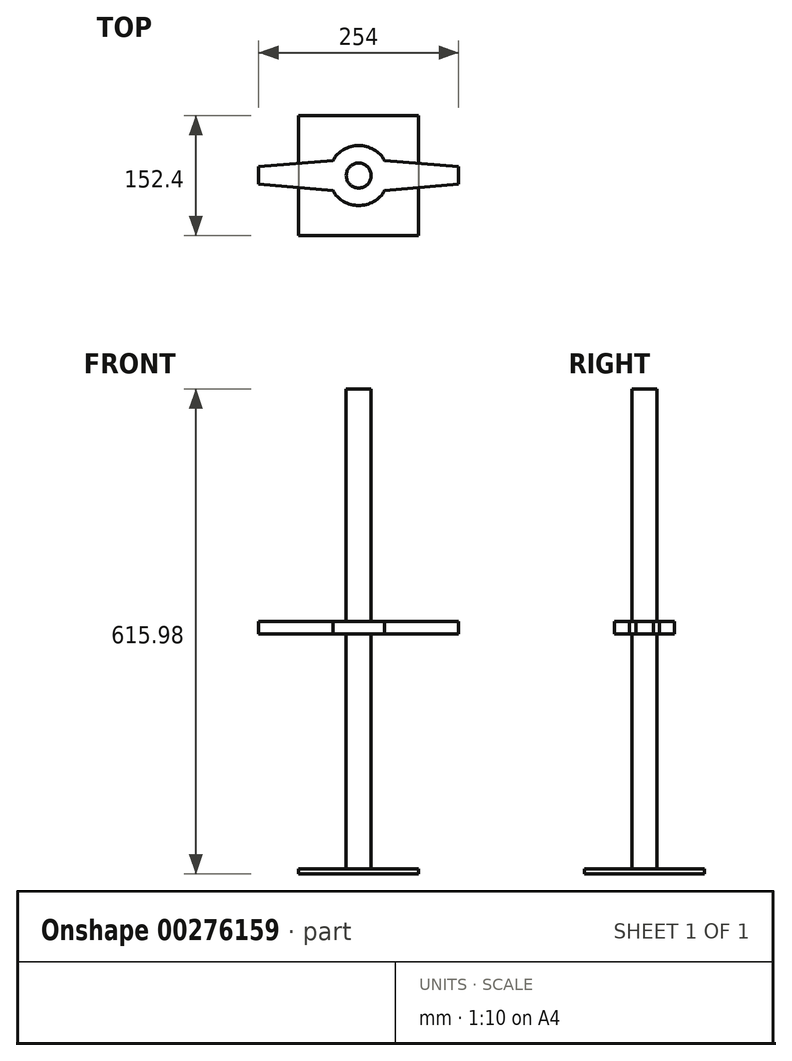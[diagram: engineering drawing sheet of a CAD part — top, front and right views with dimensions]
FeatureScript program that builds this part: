
annotation { "Feature Type Name" : "Feature", "Feature Type Description" : "" }
export const myFeature = defineFeature(function(context is Context, id is Id, definition is map)
    precondition{}
    {
        {
            var Q0;
            Q0=qCreatedBy(makeId("Top.planeOp"),FACE);
            var sketch = newSketch(context, id + "F0", { "sketchPlane" : qUnion([Q0])});
            skLineSegment(sketch, "E0.bottom", {"start": v(76.2, 76.2) * mm, "end": v(-76.2, 76.2) * mm});
            skLineSegment(sketch, "E0.top", {"start": v(76.2, -76.2) * mm, "end": v(-76.2, -76.2) * mm});
            skLineSegment(sketch, "E0.left", {"start": v(76.2, 76.2) * mm, "end": v(76.2, -76.2) * mm});
            skLineSegment(sketch, "E0.right", {"start": v(-76.2, 76.2) * mm, "end": v(-76.2, -76.2) * mm});
            skPoint(sketch, "E0.middle", {"position": v(0, 0) * mm});
            skSolve(sketch);
        }
        {
            var Q0;
            Q0 = qSketchRegion(id + "F0", true);
            extrude(context, id + "F1", {"entities" : qUnion([Q0]), "depth" : 6.38 * mm});
        }
        {
            var Q0;
            Q0=makeQuery(id+"F1.opExtrude","CAP_FACE",FACE,{"disambiguationData":[OSD([sQuery(id+"F0.wireOp",EDGE,"E0.bottom"),sQuery(id+"F0.wireOp",EDGE,"E0.top"),sQuery(id+"F0.wireOp",EDGE,"E0.left"),sQuery(id+"F0.wireOp",EDGE,"E0.right")])],"isStart":false});
            var sketch = newSketch(context, id + "F2", { "sketchPlane" : qUnion([Q0])});
            skCircle(sketch, "E1", {"center": v(0, 0) * mm, "radius": 15.88 * mm});
            skSolve(sketch);
        }
        {
            var Q0;
            Q0 = qSketchRegion(id + "F2", true);
            extrude(context, id + "F3", {"entities" : qUnion([Q0]), "operationType" : NewBodyOperationType.ADD, "depth" : 609.6 * mm});
        }
        {
            var Q0;
            Q0=qCreatedBy(makeId("Top.planeOp"),FACE);
            cPlane(context, id + "F4", {"entities" : qUnion([Q0]), "cplaneType" : CPlaneType.OFFSET, "offset" : 304.8 * mm, "width" : 152.4 * mm, "height" : 152.4 * mm});
        }
        {
            var Q0;
            Q0=qCreatedBy(id+"F4.planeOp",FACE);
            var sketch = newSketch(context, id + "F5", { "sketchPlane" : qUnion([Q0])});
            skArc(sketch, "E2", {"start": v(33, 19.05) * mm, "mid": v(0, 38.1) * mm, "end": v(-33, 19.05) * mm});
            skLineSegment(sketch, "E3", {"start": v(33, -19.05) * mm, "end": v(127, -11.11) * mm});
            skLineSegment(sketch, "E4", {"start": v(127, -11.11) * mm, "end": v(127, 11.11) * mm});
            skLineSegment(sketch, "E5", {"start": v(127, 11.11) * mm, "end": v(33, 19.05) * mm});
            skLineSegment(sketch, "E6.MirrorCS", {"start": v(-127, 11.11) * mm, "end": v(-33, 19.05) * mm});
            skLineSegment(sketch, "E7.MirrorCS", {"start": v(-127, -11.11) * mm, "end": v(-127, 11.11) * mm});
            skLineSegment(sketch, "E8.MirrorCS", {"start": v(-33, -19.05) * mm, "end": v(-127, -11.11) * mm});
            skArc(sketch, "E9.trimOffspring", {"start": v(-33, -19.05) * mm, "mid": v(0, -38.1) * mm, "end": v(33, -19.05) * mm});
            skSolve(sketch);
        }
        {
            var Q0;
            Q0 = qSketchRegion(id + "F5", true);
            extrude(context, id + "F6", {"entities" : qUnion([Q0]), "operationType" : NewBodyOperationType.ADD, "depth" : 15.88 * mm});
        }
    });
